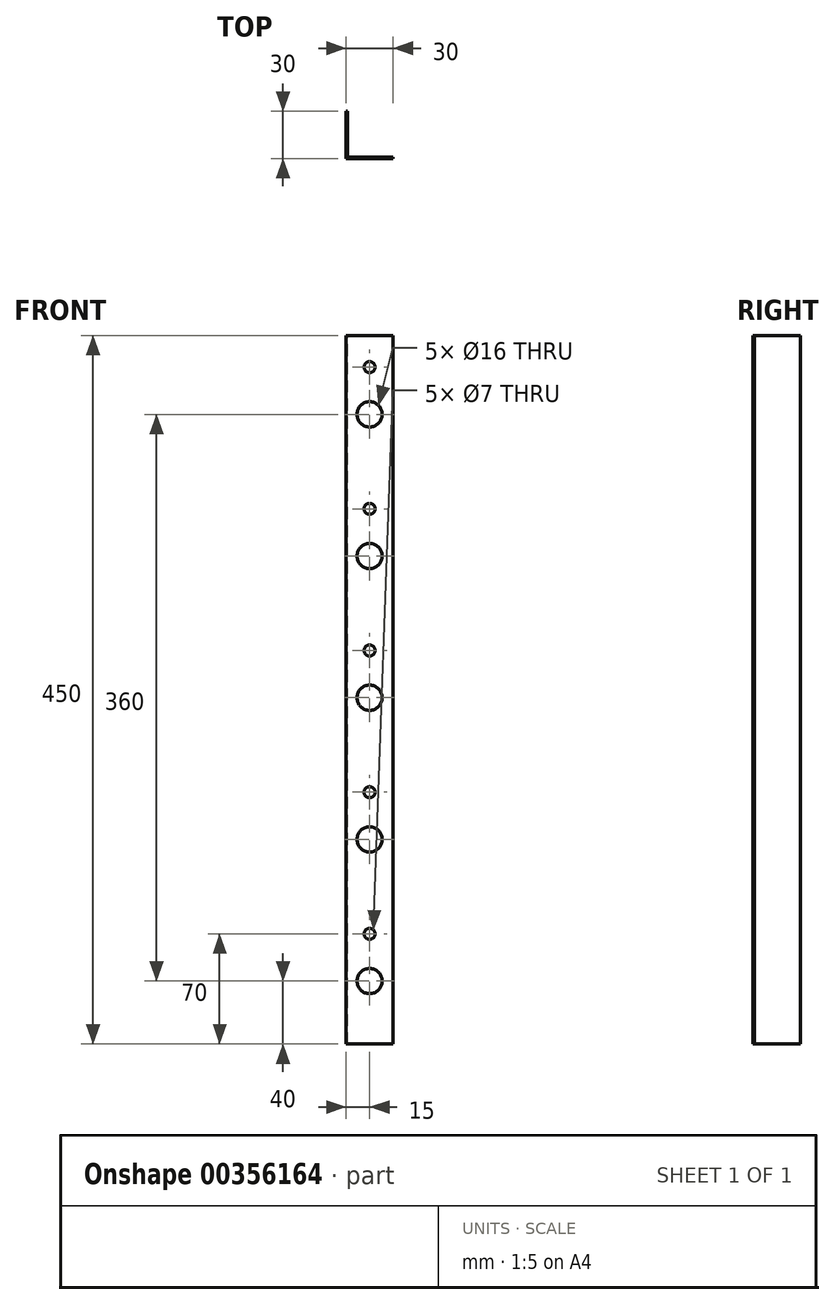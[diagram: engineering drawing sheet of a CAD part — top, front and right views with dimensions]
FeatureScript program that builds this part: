
annotation { "Feature Type Name" : "Feature", "Feature Type Description" : "" }
export const myFeature = defineFeature(function(context is Context, id is Id, definition is map)
    precondition{}
    {
        {
            var Q0;
            Q0=qCreatedBy(makeId("Top.planeOp"),FACE);
            var sketch = newSketch(context, id + "F0", { "sketchPlane" : qUnion([Q0])});
            skLineSegment(sketch, "E0.bottom", {"start": v(15, -15) * mm, "end": v(-15, -15) * mm});
            skLineSegment(sketch, "E0.top", {"start": v(-14.1, 15) * mm, "end": v(-15, 15) * mm});
            skLineSegment(sketch, "E0.left", {"start": v(15, -15) * mm, "end": v(15, -14.1) * mm});
            skLineSegment(sketch, "E0.right", {"start": v(-15, -15) * mm, "end": v(-15, 15) * mm});
            skPoint(sketch, "E0.middle", {"position": v(0, 0) * mm});
            skLineSegment(sketch, "E1", {"start": v(-14.1, 15) * mm, "end": v(-14.1, -14.1) * mm});
            skLineSegment(sketch, "E2", {"start": v(-14.1, -14.1) * mm, "end": v(15, -14.1) * mm});
            skSolve(sketch);
        }
        {
            var Q0;
            Q0 = qSketchRegion(id + "F0", true);
            extrude(context, id + "F1", {"entities" : qUnion([Q0]), "endBound" : BoundingType.SYMMETRIC, "oppositeDirection" : true, "depth" : 450 * mm});
        }
        {
            var Q0;
            Q0=makeQuery(id+"F1.opExtrude","SWEPT_FACE",FACE,{"disambiguationData":[OSD([sQuery(id+"F0.wireOp",EDGE,"E0.bottom")])]});
            var sketch = newSketch(context, id + "F2", { "sketchPlane" : qUnion([Q0])});
            skCircle(sketch, "E3", {"center": v(0, -185) * mm, "radius": 8 * mm});
            skCircle(sketch, "E4", {"center": v(0, -5) * mm, "radius": 8 * mm});
            skCircle(sketch, "E5", {"center": v(0, 85) * mm, "radius": 8 * mm});
            skCircle(sketch, "E6", {"center": v(0, 175) * mm, "radius": 8 * mm});
            skCircle(sketch, "E7", {"center": v(0, -95) * mm, "radius": 8 * mm});
            skPoint(sketch, "E8", {"position": v(0, -155) * mm});
            skPoint(sketch, "E9", {"position": v(0, -65) * mm});
            skPoint(sketch, "E10", {"position": v(0, 25) * mm});
            skPoint(sketch, "E11", {"position": v(0, 115) * mm});
            skPoint(sketch, "E12", {"position": v(0, 205) * mm});
            skSolve(sketch);
        }
        {
            var Q0;
            Q0=sQuery(id+"F2.wireOp",VERTEX,"E6.center");
            var Q1;
            Q1=sQuery(id+"F2.wireOp",VERTEX,"E5.center");
            var Q2;
            Q2=sQuery(id+"F2.wireOp",VERTEX,"E4.center");
            var Q3;
            Q3=sQuery(id+"F2.wireOp",VERTEX,"E7.center");
            var Q4;
            Q4=sQuery(id+"F2.wireOp",VERTEX,"E3.center");
            var Q5;
            Q5=makeQuery(id+"F1.opExtrude","SWEPT_BODY",BODY,{"disambiguationData":[OSD([sQuery(id+"F0.wireOp",EDGE,"E0.bottom"),sQuery(id+"F0.wireOp",EDGE,"E0.top"),sQuery(id+"F0.wireOp",EDGE,"E0.left"),sQuery(id+"F0.wireOp",EDGE,"E0.right"),sQuery(id+"F0.wireOp",EDGE,"E1"),sQuery(id+"F0.wireOp",EDGE,"E2")])]});
            hole(context, id + "F3", {"style" : HoleStyle.SIMPLE, "endStyle" : HoleEndStyle.THROUGH, "holeDiameter" : 16 * mm, "isTappedThrough" : true, "tappedDepth" : 12.7 * mm, "tapClearance" : 3, "locations" : qUnion([Q0, Q1, Q2, Q3, Q4]), "scope" : qUnion([Q5])});
        }
        {
            var Q0;
            Q0=sQuery(id+"F2.wireOp",VERTEX,"E8");
            var Q1;
            Q1=sQuery(id+"F2.wireOp",VERTEX,"E9");
            var Q2;
            Q2=sQuery(id+"F2.wireOp",VERTEX,"E10");
            var Q3;
            Q3=sQuery(id+"F2.wireOp",VERTEX,"E11");
            var Q4;
            Q4=sQuery(id+"F2.wireOp",VERTEX,"E12");
            var Q5;
            Q5=makeQuery(id+"F1.opExtrude","SWEPT_BODY",BODY,{"disambiguationData":[OSD([sQuery(id+"F0.wireOp",EDGE,"E0.bottom"),sQuery(id+"F0.wireOp",EDGE,"E0.top"),sQuery(id+"F0.wireOp",EDGE,"E0.left"),sQuery(id+"F0.wireOp",EDGE,"E0.right"),sQuery(id+"F0.wireOp",EDGE,"E1"),sQuery(id+"F0.wireOp",EDGE,"E2")])]});
            hole(context, id + "F4", {"style" : HoleStyle.SIMPLE, "endStyle" : HoleEndStyle.THROUGH, "holeDiameter" : 7 * mm, "isTappedThrough" : true, "tappedDepth" : 12.7 * mm, "tapClearance" : 3, "locations" : qUnion([Q0, Q1, Q2, Q3, Q4]), "scope" : qUnion([Q5])});
        }
    });
